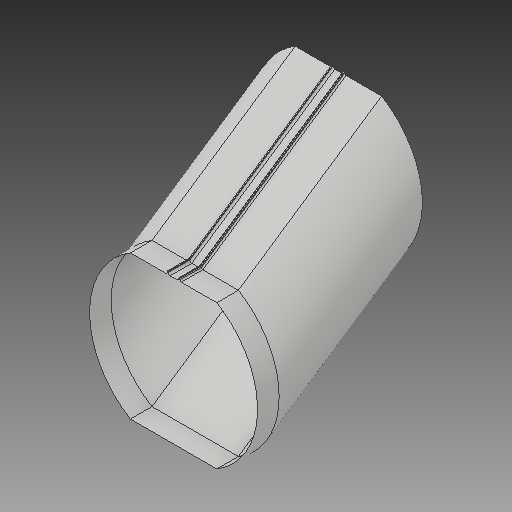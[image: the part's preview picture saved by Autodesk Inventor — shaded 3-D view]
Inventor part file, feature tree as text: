
AUTODESK INVENTOR PART (.ipt)
format: ipt  version: 2017 (Build 210142000, 142)  size: 199,168 bytes
history: native  units: in
note: dims shown in document units (in); Inventor stores cm internally (conversion verified against a paired STEP export)
features: sketch x2, plane x1, sweep x1, extrude x1, delete_face x1
ambient origin geometry x8: Origin, YZ Plane, XZ Plane, XY Plane, X Axis, Y Axis, Z Axis, Center Point
bodies: Solid1 (feature_tree)
feature tree (6):
  sketch  "Sketch1"  dims[d0=6.6667in d28=8.0in]
  plane  "Work Plane2"
  sweep  "ramp"
  extrude  "connection bottom"  Depth=0.0884in TaperAngle=0.0deg
  delete_face  "Delete Face1"
  sketch  "Sketch6"  dims[d30=0.0in d31=0.0in d32=1.0in d33=0.0in d62=0.8521in d110=4.0in d111=0.5833in d112=3.8873in d113=3.8873in d114=1.7083in d115=0.0625in d116=0.0625in d117=1.6458in d118=0.25in d119=0.125in d121=0.0884in d122=45.0deg d123=3.3333in d124=0.125in d125=4.0in d126=0.5833in d127=3.8873in d128=3.8873in d129=1.7083in d130=0.0625in d131=0.0625in d132=1.6458in d133=0.25in d134=0.125in d136=0.0884in d137=45.0deg d138=3.3333in d139=0.125in]
